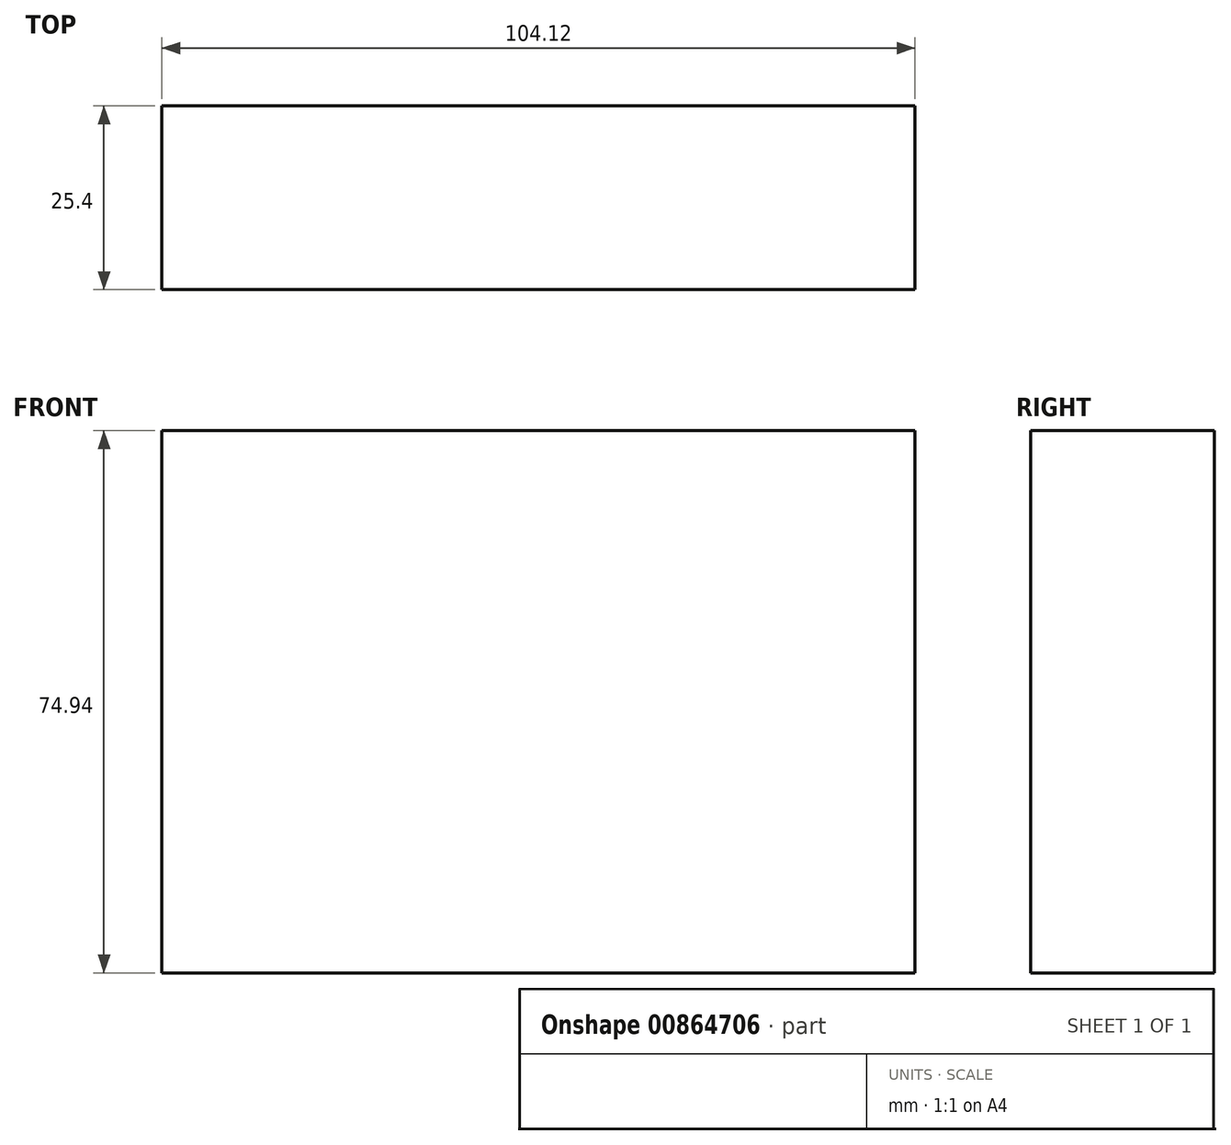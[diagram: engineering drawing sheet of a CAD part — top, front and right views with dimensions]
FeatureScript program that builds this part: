
annotation { "Feature Type Name" : "Feature", "Feature Type Description" : "" }
export const myFeature = defineFeature(function(context is Context, id is Id, definition is map)
    precondition{}
    {
        {
            var Q0;
            Q0=qCreatedBy(makeId("Front.planeOp"),FACE);
            var sketch = newSketch(context, id + "F0", { "sketchPlane" : qUnion([Q0])});
            skLineSegment(sketch, "E0", {"start": v(-53.5, 38.37) * mm, "end": v(50.62, 38.37) * mm});
            skLineSegment(sketch, "E1", {"start": v(50.62, 38.37) * mm, "end": v(50.62, -36.57) * mm});
            skLineSegment(sketch, "E2", {"start": v(50.62, -36.57) * mm, "end": v(-53.5, -36.57) * mm});
            skLineSegment(sketch, "E3", {"start": v(-53.5, -36.57) * mm, "end": v(-53.5, 38.37) * mm});
            skSolve(sketch);
        }
        {
            var Q0;
            Q0 = qSketchRegion(id + "F0", true);
            extrude(context, id + "F1", {"entities" : qUnion([Q0]), "depth" : 25.4 * mm, "offsetDistance" : 25.4 * mm});
        }
    });
